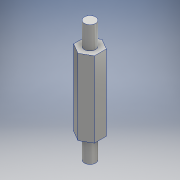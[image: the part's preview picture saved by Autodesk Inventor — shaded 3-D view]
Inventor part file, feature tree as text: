
AUTODESK INVENTOR PART (.ipt)
format: ipt  version: 2016 (Build 200138000, 138)  size: 104,448 bytes
history: native  units: mm
features: extrude x3, sketch x2, other x1
ambient origin geometry x8: Origin, YZ Plane, XZ Plane, XY Plane, X Axis, Y Axis, Z Axis, Center Point
bodies: Body1 (feature_tree)
feature tree (6):
  other  "ソリッド1"
  sketch  "スケッチ1"
  extrude  "押し出し1"  Depth=5.5mm
  extrude  "押し出し2"  Depth=3.0mm
  extrude  "押し出し3"  Depth=20.0mm TaperAngle=0.0deg
  sketch  "スケッチ2"
